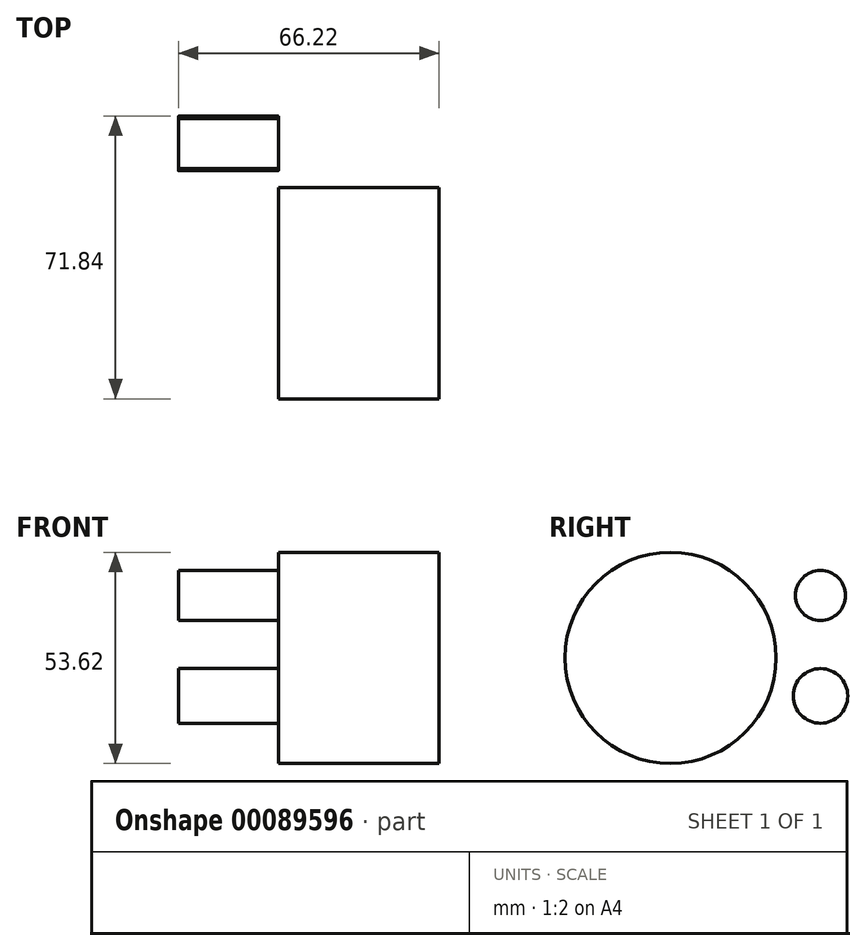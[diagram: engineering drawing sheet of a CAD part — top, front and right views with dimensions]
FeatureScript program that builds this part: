
annotation { "Feature Type Name" : "Feature", "Feature Type Description" : "" }
export const myFeature = defineFeature(function(context is Context, id is Id, definition is map)
    precondition{}
    {
        {
            var Q0;
            Q0=qCreatedBy(makeId("Right.planeOp"),FACE);
            var sketch = newSketch(context, id + "F0", { "sketchPlane" : qUnion([Q0])});
            skLineSegment(sketch, "E0", {"start": v(-50.8, 25.4) * mm, "end": v(50.8, 25.4) * mm});
            skLineSegment(sketch, "E1", {"start": v(50.8, 25.4) * mm, "end": v(50.8, -25.4) * mm});
            skLineSegment(sketch, "E2", {"start": v(50.8, -25.4) * mm, "end": v(-50.8, -25.4) * mm});
            skLineSegment(sketch, "E3", {"start": v(-50.8, -25.4) * mm, "end": v(-50.8, 25.4) * mm});
            skSolve(sketch);
        }
        {
            var Q0;
            Q0=makeQuery(id+"F0.imprint","IMPRINT",FACE,{"disambiguationData":[TD([[makeQuery(id+"F0.imprint","IMPRINT",EDGE,{"derivedFrom":sQuery(id+"F0.wireOp",EDGE,"E0")}),-1.0]])]});
            extrude(context, id + "F1", {"entities" : qUnion([Q0]), "depth" : 25.4 * mm});
        }
        {
            var Q0;
            Q0=makeQuery(id+"F1.opExtrude","CAP_FACE",FACE,{"disambiguationData":[OSD([sQuery(id+"F0.wireOp",EDGE,"E0"),sQuery(id+"F0.wireOp",EDGE,"E1"),sQuery(id+"F0.wireOp",EDGE,"E2"),sQuery(id+"F0.wireOp",EDGE,"E3")])],"isStart":false});
            var sketch = newSketch(context, id + "F2", { "sketchPlane" : qUnion([Q0])});
            skCircle(sketch, "E4", {"center": v(-38.1, 15.86) * mm, "radius": 6.35 * mm});
            skCircle(sketch, "E5", {"center": v(-38.1, -9.67) * mm, "radius": 6.93 * mm});
            skCircle(sketch, "E6.MirrorC", {"center": v(38.1, 15.86) * mm, "radius": 6.35 * mm});
            skCircle(sketch, "E7.MirrorC", {"center": v(38.1, -9.67) * mm, "radius": 6.93 * mm});
            skSolve(sketch);
        }
        {
            var Q0;
            Q0=makeQuery(id+"F2.imprint","IMPRINT",FACE,{"disambiguationData":[TD([[makeQuery(id+"F2.imprint","IMPRINT",EDGE,{"derivedFrom":sQuery(id+"F2.wireOp",EDGE,"E4")}),1.0]])]});
            var Q1;
            Q1=makeQuery(id+"F2.imprint","IMPRINT",FACE,{"disambiguationData":[TD([[makeQuery(id+"F2.imprint","IMPRINT",EDGE,{"derivedFrom":sQuery(id+"F2.wireOp",EDGE,"E6.MirrorC")}),-1.0]])]});
            var Q2;
            Q2=makeQuery(id+"F2.imprint","IMPRINT",FACE,{"disambiguationData":[TD([[makeQuery(id+"F2.imprint","IMPRINT",EDGE,{"derivedFrom":sQuery(id+"F2.wireOp",EDGE,"E7.MirrorC")}),-1.0]])]});
            var Q3;
            Q3=makeQuery(id+"F2.imprint","IMPRINT",FACE,{"disambiguationData":[TD([[makeQuery(id+"F2.imprint","IMPRINT",EDGE,{"derivedFrom":sQuery(id+"F2.wireOp",EDGE,"E5")}),1.0]])]});
            extrude(context, id + "F3", {"entities" : qUnion([Q0, Q1, Q2, Q3]), "operationType" : NewBodyOperationType.REMOVE, "endBound" : BoundingType.THROUGH_ALL, "oppositeDirection" : true, "depth" : 25.4 * mm});
        }
        {
            var Q0;
            Q0=qCreatedBy(makeId("Top.planeOp"),FACE);
            var sketch = newSketch(context, id + "F4", { "sketchPlane" : qUnion([Q0])});
            skLineSegment(sketch, "E8", {"start": v(25.4, -26.81) * mm, "end": v(66.22, -26.81) * mm});
            skLineSegment(sketch, "E9", {"start": v(66.22, -26.81) * mm, "end": v(66.22, 0) * mm});
            skLineSegment(sketch, "E10", {"start": v(25.4, 0) * mm, "end": v(25.4, -26.81) * mm});
            skLineSegment(sketch, "E11", {"start": v(66.22, 0) * mm, "end": v(25.4, 0) * mm});
            skSolve(sketch);
        }
        {
            var Q0;
            Q0 = qSketchRegion(id + "F4", true);
            var Q1;
            Q1=sQuery(id+"F4.wireOp",EDGE,"E11");
            revolve(context, id + "F5", {"operationType" : NewBodyOperationType.ADD, "entities" : qUnion([Q0]), "axis" : qUnion([Q1]), "revolveType" : RevolveType.FULL});
        }
    });
